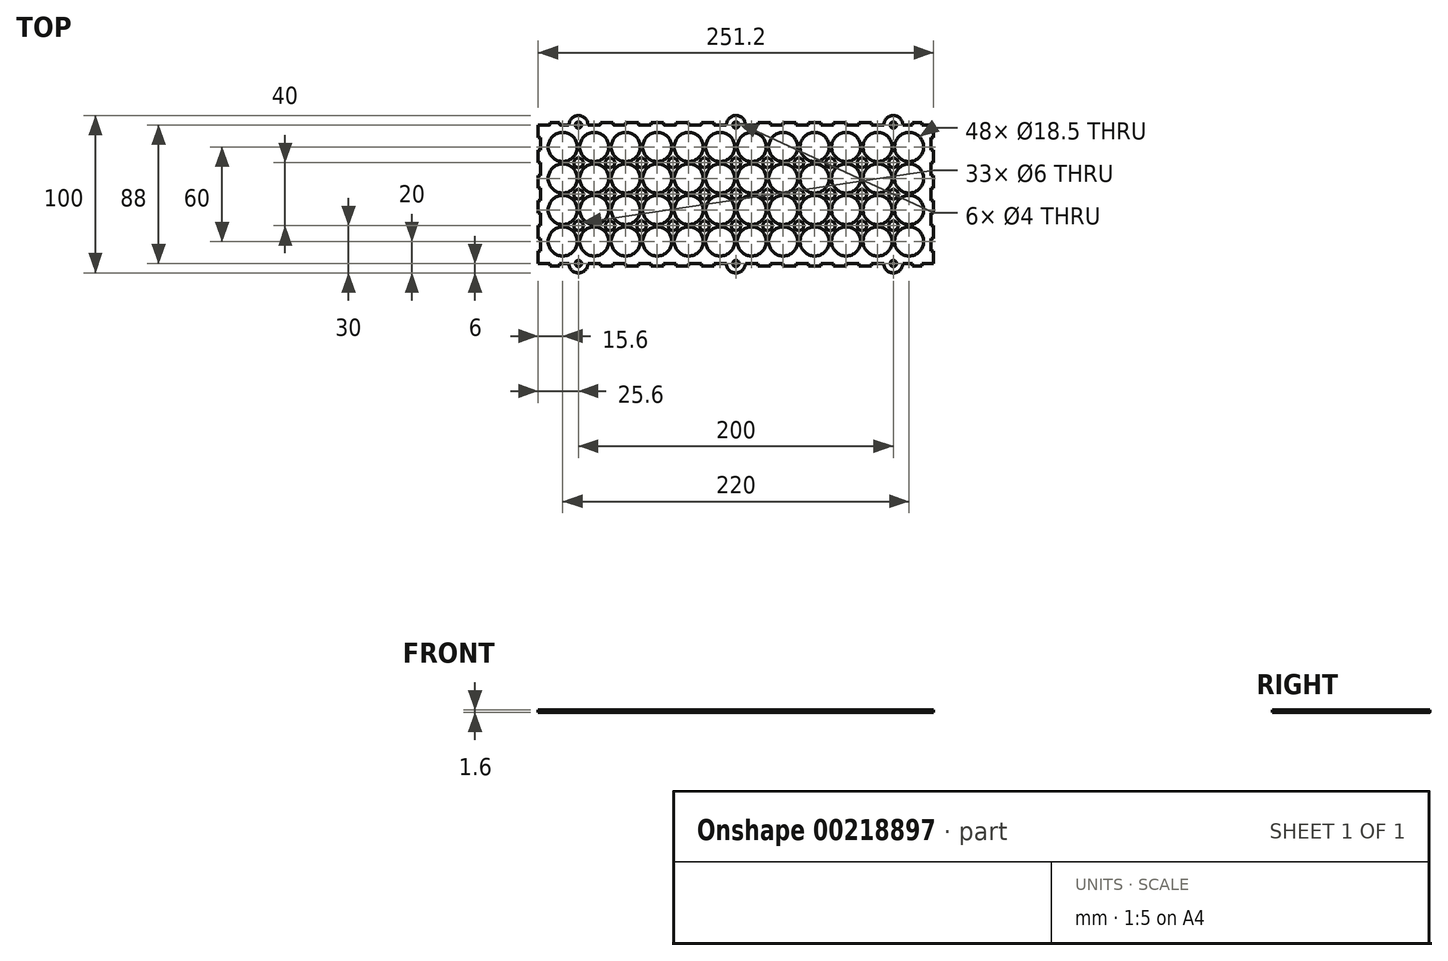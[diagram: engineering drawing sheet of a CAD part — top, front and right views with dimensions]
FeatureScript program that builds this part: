
annotation { "Feature Type Name" : "Feature", "Feature Type Description" : "" }
export const myFeature = defineFeature(function(context is Context, id is Id, definition is map)
    precondition{}
    {
        {
            var Q0;
            Q0=qCreatedBy(makeId("Top.planeOp"),FACE);
            var sketch = newSketch(context, id + "F0", { "sketchPlane" : qUnion([Q0])});
            skCircle(sketch, "E0", {"center": v(-110, -30) * mm, "radius": 9.25 * mm});
            skCircle(sketch, "E1.0.1.0", {"center": v(-110, -10) * mm, "radius": 9.25 * mm});
            skCircle(sketch, "E1.0.2.0", {"center": v(-110, 10) * mm, "radius": 9.25 * mm});
            skCircle(sketch, "E1.0.3.0", {"center": v(-110, 30) * mm, "radius": 9.25 * mm});
            skCircle(sketch, "E1.1.0.0", {"center": v(-90, -30) * mm, "radius": 9.25 * mm});
            skCircle(sketch, "E1.1.1.0", {"center": v(-90, -10) * mm, "radius": 9.25 * mm});
            skCircle(sketch, "E1.1.2.0", {"center": v(-90, 10) * mm, "radius": 9.25 * mm});
            skCircle(sketch, "E1.1.3.0", {"center": v(-90, 30) * mm, "radius": 9.25 * mm});
            skCircle(sketch, "E1.2.0.0", {"center": v(-70, -30) * mm, "radius": 9.25 * mm});
            skCircle(sketch, "E1.2.1.0", {"center": v(-70, -10) * mm, "radius": 9.25 * mm});
            skCircle(sketch, "E1.2.2.0", {"center": v(-70, 10) * mm, "radius": 9.25 * mm});
            skCircle(sketch, "E1.2.3.0", {"center": v(-70, 30) * mm, "radius": 9.25 * mm});
            skCircle(sketch, "E1.3.0.0", {"center": v(-50, -30) * mm, "radius": 9.25 * mm});
            skCircle(sketch, "E1.3.1.0", {"center": v(-50, -10) * mm, "radius": 9.25 * mm});
            skCircle(sketch, "E1.3.2.0", {"center": v(-50, 10) * mm, "radius": 9.25 * mm});
            skCircle(sketch, "E1.3.3.0", {"center": v(-50, 30) * mm, "radius": 9.25 * mm});
            skCircle(sketch, "E1.4.0.0", {"center": v(-30, -30) * mm, "radius": 9.25 * mm});
            skCircle(sketch, "E1.4.1.0", {"center": v(-30, -10) * mm, "radius": 9.25 * mm});
            skCircle(sketch, "E1.4.2.0", {"center": v(-30, 10) * mm, "radius": 9.25 * mm});
            skCircle(sketch, "E1.4.3.0", {"center": v(-30, 30) * mm, "radius": 9.25 * mm});
            skCircle(sketch, "E1.5.0.0", {"center": v(-10, -30) * mm, "radius": 9.25 * mm});
            skCircle(sketch, "E1.5.1.0", {"center": v(-10, -10) * mm, "radius": 9.25 * mm});
            skCircle(sketch, "E1.5.2.0", {"center": v(-10, 10) * mm, "radius": 9.25 * mm});
            skCircle(sketch, "E1.5.3.0", {"center": v(-10, 30) * mm, "radius": 9.25 * mm});
            skCircle(sketch, "E1.6.0.0", {"center": v(10, -30) * mm, "radius": 9.25 * mm});
            skCircle(sketch, "E1.6.1.0", {"center": v(10, -10) * mm, "radius": 9.25 * mm});
            skCircle(sketch, "E1.6.2.0", {"center": v(10, 10) * mm, "radius": 9.25 * mm});
            skCircle(sketch, "E1.6.3.0", {"center": v(10, 30) * mm, "radius": 9.25 * mm});
            skCircle(sketch, "E1.7.0.0", {"center": v(30, -30) * mm, "radius": 9.25 * mm});
            skCircle(sketch, "E1.7.1.0", {"center": v(30, -10) * mm, "radius": 9.25 * mm});
            skCircle(sketch, "E1.7.2.0", {"center": v(30, 10) * mm, "radius": 9.25 * mm});
            skCircle(sketch, "E1.7.3.0", {"center": v(30, 30) * mm, "radius": 9.25 * mm});
            skCircle(sketch, "E1.8.0.0", {"center": v(50, -30) * mm, "radius": 9.25 * mm});
            skCircle(sketch, "E1.8.1.0", {"center": v(50, -10) * mm, "radius": 9.25 * mm});
            skCircle(sketch, "E1.8.2.0", {"center": v(50, 10) * mm, "radius": 9.25 * mm});
            skCircle(sketch, "E1.8.3.0", {"center": v(50, 30) * mm, "radius": 9.25 * mm});
            skCircle(sketch, "E1.9.0.0", {"center": v(70, -30) * mm, "radius": 9.25 * mm});
            skCircle(sketch, "E1.9.1.0", {"center": v(70, -10) * mm, "radius": 9.25 * mm});
            skCircle(sketch, "E1.9.2.0", {"center": v(70, 10) * mm, "radius": 9.25 * mm});
            skCircle(sketch, "E1.9.3.0", {"center": v(70, 30) * mm, "radius": 9.25 * mm});
            skCircle(sketch, "E1.10.0.0", {"center": v(90, -30) * mm, "radius": 9.25 * mm});
            skCircle(sketch, "E1.10.1.0", {"center": v(90, -10) * mm, "radius": 9.25 * mm});
            skCircle(sketch, "E1.10.2.0", {"center": v(90, 10) * mm, "radius": 9.25 * mm});
            skCircle(sketch, "E1.10.3.0", {"center": v(90, 30) * mm, "radius": 9.25 * mm});
            skCircle(sketch, "E1.11.0.0", {"center": v(110, -30) * mm, "radius": 9.25 * mm});
            skCircle(sketch, "E1.11.1.0", {"center": v(110, -10) * mm, "radius": 9.25 * mm});
            skCircle(sketch, "E1.11.2.0", {"center": v(110, 10) * mm, "radius": 9.25 * mm});
            skCircle(sketch, "E1.11.3.0", {"center": v(110, 30) * mm, "radius": 9.25 * mm});
            skLineSegment(sketch, "E1.direction1", {"start": v(-110, -30) * mm, "end": v(-90, -30) * mm, "construction": true});
            skLineSegment(sketch, "E1.direction2", {"start": v(-110, -30) * mm, "end": v(-110, -10) * mm, "construction": true});
            skCircle(sketch, "E2", {"center": v(-100, -20) * mm, "radius": 3 * mm});
            skCircle(sketch, "E3.0.1.0", {"center": v(-100, 0) * mm, "radius": 3 * mm});
            skCircle(sketch, "E3.0.2.0", {"center": v(-100, 20) * mm, "radius": 3 * mm});
            skCircle(sketch, "E3.1.0.0", {"center": v(-80, -20) * mm, "radius": 3 * mm});
            skCircle(sketch, "E3.1.1.0", {"center": v(-80, 0) * mm, "radius": 3 * mm});
            skCircle(sketch, "E3.1.2.0", {"center": v(-80, 20) * mm, "radius": 3 * mm});
            skCircle(sketch, "E3.2.0.0", {"center": v(-60, -20) * mm, "radius": 3 * mm});
            skCircle(sketch, "E3.2.1.0", {"center": v(-60, 0) * mm, "radius": 3 * mm});
            skCircle(sketch, "E3.2.2.0", {"center": v(-60, 20) * mm, "radius": 3 * mm});
            skCircle(sketch, "E3.3.0.0", {"center": v(-40, -20) * mm, "radius": 3 * mm});
            skCircle(sketch, "E3.3.1.0", {"center": v(-40, 0) * mm, "radius": 3 * mm});
            skCircle(sketch, "E3.3.2.0", {"center": v(-40, 20) * mm, "radius": 3 * mm});
            skCircle(sketch, "E3.4.0.0", {"center": v(-20, -20) * mm, "radius": 3 * mm});
            skCircle(sketch, "E3.4.1.0", {"center": v(-20, 0) * mm, "radius": 3 * mm});
            skCircle(sketch, "E3.4.2.0", {"center": v(-20, 20) * mm, "radius": 3 * mm});
            skCircle(sketch, "E3.5.0.0", {"center": v(0, -20) * mm, "radius": 3 * mm});
            skCircle(sketch, "E3.5.1.0", {"center": v(0, 0) * mm, "radius": 3 * mm});
            skCircle(sketch, "E3.5.2.0", {"center": v(0, 20) * mm, "radius": 3 * mm});
            skCircle(sketch, "E3.6.0.0", {"center": v(20, -20) * mm, "radius": 3 * mm});
            skCircle(sketch, "E3.6.1.0", {"center": v(20, 0) * mm, "radius": 3 * mm});
            skCircle(sketch, "E3.6.2.0", {"center": v(20, 20) * mm, "radius": 3 * mm});
            skCircle(sketch, "E3.7.0.0", {"center": v(40, -20) * mm, "radius": 3 * mm});
            skCircle(sketch, "E3.7.1.0", {"center": v(40, 0) * mm, "radius": 3 * mm});
            skCircle(sketch, "E3.7.2.0", {"center": v(40, 20) * mm, "radius": 3 * mm});
            skCircle(sketch, "E3.8.0.0", {"center": v(60, -20) * mm, "radius": 3 * mm});
            skCircle(sketch, "E3.8.1.0", {"center": v(60, 0) * mm, "radius": 3 * mm});
            skCircle(sketch, "E3.8.2.0", {"center": v(60, 20) * mm, "radius": 3 * mm});
            skCircle(sketch, "E3.9.0.0", {"center": v(80, -20) * mm, "radius": 3 * mm});
            skCircle(sketch, "E3.9.1.0", {"center": v(80, 0) * mm, "radius": 3 * mm});
            skCircle(sketch, "E3.9.2.0", {"center": v(80, 20) * mm, "radius": 3 * mm});
            skCircle(sketch, "E3.10.0.0", {"center": v(100, -20) * mm, "radius": 3 * mm});
            skCircle(sketch, "E3.10.1.0", {"center": v(100, 0) * mm, "radius": 3 * mm});
            skCircle(sketch, "E3.10.2.0", {"center": v(100, 20) * mm, "radius": 3 * mm});
            skLineSegment(sketch, "E3.direction1", {"start": v(-100, -20) * mm, "end": v(-80, -20) * mm, "construction": true});
            skLineSegment(sketch, "E3.direction2", {"start": v(-100, -20) * mm, "end": v(-100, 0) * mm, "construction": true});
            skLineSegment(sketch, "E4", {"start": v(-132.11, 0) * mm, "end": v(153.17, 0) * mm, "construction": true});
            skLineSegment(sketch, "E5", {"start": v(0, 71.44) * mm, "end": v(0, -47.17) * mm, "construction": true});
            skCircle(sketch, "E6", {"center": v(0, 44) * mm, "radius": 2 * mm});
            skLineSegment(sketch, "E7", {"start": v(-100, 72.52) * mm, "end": v(-100, -46.79) * mm, "construction": true});
            skLineSegment(sketch, "E8.MirrorCS", {"start": v(100, 72.52) * mm, "end": v(100, -46.79) * mm, "construction": true});
            skCircle(sketch, "E9", {"center": v(-100, 44) * mm, "radius": 2 * mm});
            skCircle(sketch, "E10.MirrorC", {"center": v(100, 44) * mm, "radius": 2 * mm});
            skArc(sketch, "E11", {"start": v(-105.98, 44.46) * mm, "mid": v(-100, 50) * mm, "end": v(-94.02, 44.46) * mm});
            skArc(sketch, "E12.MirrorCS", {"start": v(106, 44) * mm, "mid": v(100, 50) * mm, "end": v(94, 44) * mm});
            skArc(sketch, "E13", {"start": v(-5.98, 44.46) * mm, "mid": v(0.23, 50) * mm, "end": v(6, 44) * mm});
            skLineSegment(sketch, "E14", {"start": v(-106.48, 44) * mm, "end": v(-111.5, 44) * mm});
            skLineSegment(sketch, "E15", {"start": v(-93.52, 44) * mm, "end": v(-86.5, 44) * mm});
            skLineSegment(sketch, "E16", {"start": v(-118, 44.5) * mm, "end": v(-118, 45.6) * mm});
            skLineSegment(sketch, "E17", {"start": v(-118, 45.6) * mm, "end": v(-112, 45.6) * mm});
            skLineSegment(sketch, "E18", {"start": v(-112, 45.6) * mm, "end": v(-112, 44.5) * mm});
            skLineSegment(sketch, "E19", {"start": v(-86, 44.5) * mm, "end": v(-86, 45.6) * mm});
            skLineSegment(sketch, "E20", {"start": v(-86, 45.6) * mm, "end": v(-78, 45.6) * mm});
            skLineSegment(sketch, "E21", {"start": v(-78, 45.6) * mm, "end": v(-78, 44.5) * mm});
            skLineSegment(sketch, "E22.1.0.0", {"start": v(-77.5, 44) * mm, "end": v(-70.5, 44) * mm});
            skLineSegment(sketch, "E22.1.0.1", {"start": v(-70, 44.5) * mm, "end": v(-70, 45.6) * mm});
            skLineSegment(sketch, "E22.1.0.2", {"start": v(-70, 45.6) * mm, "end": v(-62, 45.6) * mm});
            skLineSegment(sketch, "E22.1.0.3", {"start": v(-62, 45.6) * mm, "end": v(-62, 44.5) * mm});
            skLineSegment(sketch, "E22.2.0.0", {"start": v(-61.5, 44) * mm, "end": v(-54, 44) * mm});
            skLineSegment(sketch, "E22.2.0.1", {"start": v(-54, 44) * mm, "end": v(-54, 45.6) * mm});
            skLineSegment(sketch, "E22.2.0.2", {"start": v(-54, 45.6) * mm, "end": v(-46, 45.6) * mm});
            skLineSegment(sketch, "E22.2.0.3", {"start": v(-46, 45.6) * mm, "end": v(-46, 44.5) * mm});
            skLineSegment(sketch, "E22.3.0.0", {"start": v(-45.5, 44) * mm, "end": v(-38.5, 44) * mm});
            skLineSegment(sketch, "E22.3.0.1", {"start": v(-38, 44.5) * mm, "end": v(-38, 45.6) * mm});
            skLineSegment(sketch, "E22.3.0.2", {"start": v(-38, 45.6) * mm, "end": v(-30, 45.6) * mm});
            skLineSegment(sketch, "E22.3.0.3", {"start": v(-30, 45.6) * mm, "end": v(-30, 44.5) * mm});
            skLineSegment(sketch, "E22.4.0.0", {"start": v(-29.5, 44) * mm, "end": v(-22.5, 44) * mm});
            skLineSegment(sketch, "E22.4.0.1", {"start": v(-22, 44.5) * mm, "end": v(-22, 45.6) * mm});
            skLineSegment(sketch, "E22.4.0.2", {"start": v(-22, 45.6) * mm, "end": v(-14, 45.6) * mm});
            skLineSegment(sketch, "E22.4.0.3", {"start": v(-14, 45.6) * mm, "end": v(-14, 44.5) * mm});
            skLineSegment(sketch, "E22.direction1", {"start": v(-94, 44) * mm, "end": v(-78, 44) * mm, "construction": true});
            skLineSegment(sketch, "E23", {"start": v(-13.5, 44) * mm, "end": v(-6.48, 44) * mm});
            skLineSegment(sketch, "E24.MirrorCS", {"start": v(30, 45.6) * mm, "end": v(30, 44) * mm});
            skLineSegment(sketch, "E25.MirrorCS", {"start": v(38, 44) * mm, "end": v(38, 45.6) * mm});
            skLineSegment(sketch, "E26.MirrorCS", {"start": v(54, 44) * mm, "end": v(54, 45.6) * mm});
            skLineSegment(sketch, "E27.MirrorCS", {"start": v(14, 45.6) * mm, "end": v(14, 44.5) * mm});
            skLineSegment(sketch, "E28.MirrorCS", {"start": v(78, 45.6) * mm, "end": v(78, 44) * mm});
            skLineSegment(sketch, "E29.MirrorCS", {"start": v(46, 45.6) * mm, "end": v(46, 44) * mm});
            skLineSegment(sketch, "E30.MirrorCS", {"start": v(62, 45.6) * mm, "end": v(62, 44) * mm});
            skLineSegment(sketch, "E31.MirrorCS", {"start": v(86, 44) * mm, "end": v(86, 45.6) * mm});
            skLineSegment(sketch, "E32.MirrorCS", {"start": v(22, 44) * mm, "end": v(22, 45.6) * mm});
            skLineSegment(sketch, "E33.MirrorCS", {"start": v(70, 44) * mm, "end": v(70, 45.6) * mm});
            skLineSegment(sketch, "E34.MirrorCS", {"start": v(94, 44) * mm, "end": v(86, 44) * mm});
            skLineSegment(sketch, "E35.MirrorCS", {"start": v(38, 45.6) * mm, "end": v(30, 45.6) * mm});
            skLineSegment(sketch, "E36.MirrorCS", {"start": v(30, 44) * mm, "end": v(22, 44) * mm});
            skLineSegment(sketch, "E37.MirrorCS", {"start": v(22, 45.6) * mm, "end": v(14, 45.6) * mm});
            skLineSegment(sketch, "E38.MirrorCS", {"start": v(62, 44) * mm, "end": v(54, 44) * mm});
            skLineSegment(sketch, "E39.MirrorCS", {"start": v(70, 45.6) * mm, "end": v(62, 45.6) * mm});
            skLineSegment(sketch, "E40.MirrorCS", {"start": v(46, 44) * mm, "end": v(38, 44) * mm});
            skLineSegment(sketch, "E41.MirrorCS", {"start": v(78, 44) * mm, "end": v(70, 44) * mm});
            skLineSegment(sketch, "E42.MirrorCS", {"start": v(86, 45.6) * mm, "end": v(78, 45.6) * mm});
            skLineSegment(sketch, "E43.MirrorCS", {"start": v(13.5, 44) * mm, "end": v(6, 44) * mm});
            skLineSegment(sketch, "E44.MirrorCS", {"start": v(54, 45.6) * mm, "end": v(46, 45.6) * mm});
            skLineSegment(sketch, "E45.MirrorCS", {"start": v(14, 45.6) * mm, "end": v(14, 44) * mm});
            skLineSegment(sketch, "E46.MirrorCS", {"start": v(14, 44) * mm, "end": v(6, 44) * mm});
            skLineSegment(sketch, "E47.MirrorCS", {"start": v(94, 44) * mm, "end": v(78, 44) * mm, "construction": true});
            skLineSegment(sketch, "E48", {"start": v(-118.5, 44) * mm, "end": v(-124, 44) * mm});
            skLineSegment(sketch, "E49.MirrorCS", {"start": v(118, 45.6) * mm, "end": v(112, 45.6) * mm});
            skLineSegment(sketch, "E50.MirrorCS", {"start": v(118, 44) * mm, "end": v(118, 45.6) * mm});
            skLineSegment(sketch, "E51.MirrorCS", {"start": v(112, 45.6) * mm, "end": v(112, 44) * mm});
            skLineSegment(sketch, "E52.MirrorCS", {"start": v(106, 44) * mm, "end": v(112, 44) * mm});
            skLineSegment(sketch, "E53.MirrorCS", {"start": v(118, 44) * mm, "end": v(124, 44) * mm});
            skLineSegment(sketch, "E54.MirrorCS", {"start": v(78, -45.6) * mm, "end": v(78, -44) * mm});
            skLineSegment(sketch, "E55.MirrorCS", {"start": v(86, -44) * mm, "end": v(86, -45.6) * mm});
            skLineSegment(sketch, "E56.MirrorCS", {"start": v(22, -44) * mm, "end": v(22, -45.6) * mm});
            skLineSegment(sketch, "E57.MirrorCS", {"start": v(70, -44) * mm, "end": v(70, -45.6) * mm});
            skLineSegment(sketch, "E58.MirrorCS", {"start": v(46, -45.6) * mm, "end": v(46, -44) * mm});
            skLineSegment(sketch, "E59.MirrorCS", {"start": v(62, -45.6) * mm, "end": v(62, -44) * mm});
            skLineSegment(sketch, "E60.MirrorCS", {"start": v(14, -45.6) * mm, "end": v(14, -44) * mm});
            skLineSegment(sketch, "E61.MirrorCS", {"start": v(54, -44) * mm, "end": v(54, -45.6) * mm});
            skLineSegment(sketch, "E62.MirrorCS", {"start": v(30, -45.6) * mm, "end": v(30, -44) * mm});
            skLineSegment(sketch, "E63.MirrorCS", {"start": v(38, -44) * mm, "end": v(38, -45.6) * mm});
            skLineSegment(sketch, "E64.MirrorCS", {"start": v(-78, -45.6) * mm, "end": v(-78, -44) * mm});
            skLineSegment(sketch, "E65.MirrorCS", {"start": v(-30, -45.6) * mm, "end": v(-30, -44) * mm});
            skLineSegment(sketch, "E66.MirrorCS", {"start": v(94, -44) * mm, "end": v(86, -44) * mm});
            skLineSegment(sketch, "E67.MirrorCS", {"start": v(-112, -45.6) * mm, "end": v(-112, -44) * mm});
            skLineSegment(sketch, "E68.MirrorCS", {"start": v(-22, -44) * mm, "end": v(-22, -45.6) * mm});
            skLineSegment(sketch, "E69.MirrorCS", {"start": v(-86, -44) * mm, "end": v(-86, -45.6) * mm});
            skLineSegment(sketch, "E70.MirrorCS", {"start": v(-46, -45.6) * mm, "end": v(-46, -44) * mm});
            skLineSegment(sketch, "E71.MirrorCS", {"start": v(-70, -44) * mm, "end": v(-70, -45.6) * mm});
            skLineSegment(sketch, "E72.MirrorCS", {"start": v(118, -44) * mm, "end": v(118, -45.6) * mm});
            skLineSegment(sketch, "E73.MirrorCS", {"start": v(112, -45.6) * mm, "end": v(112, -44) * mm});
            skLineSegment(sketch, "E74.MirrorCS", {"start": v(-38, -44) * mm, "end": v(-38, -45.6) * mm});
            skLineSegment(sketch, "E75.MirrorCS", {"start": v(-14, -45.6) * mm, "end": v(-14, -44) * mm});
            skLineSegment(sketch, "E76.MirrorCS", {"start": v(-62, -45.6) * mm, "end": v(-62, -44) * mm});
            skLineSegment(sketch, "E77.MirrorCS", {"start": v(-118, -44) * mm, "end": v(-118, -45.6) * mm});
            skLineSegment(sketch, "E78.MirrorCS", {"start": v(-54, -44) * mm, "end": v(-54, -45.6) * mm});
            skLineSegment(sketch, "E79.MirrorCS", {"start": v(54, -45.6) * mm, "end": v(46, -45.6) * mm});
            skLineSegment(sketch, "E80.MirrorCS", {"start": v(38, -45.6) * mm, "end": v(30, -45.6) * mm});
            skLineSegment(sketch, "E81.MirrorCS", {"start": v(62, -44) * mm, "end": v(54, -44) * mm});
            skLineSegment(sketch, "E82.MirrorCS", {"start": v(-94, -44) * mm, "end": v(-86, -44) * mm});
            skLineSegment(sketch, "E83.MirrorCS", {"start": v(30, -44) * mm, "end": v(22, -44) * mm});
            skLineSegment(sketch, "E84.MirrorCS", {"start": v(86, -45.6) * mm, "end": v(78, -45.6) * mm});
            skLineSegment(sketch, "E85.MirrorCS", {"start": v(70, -45.6) * mm, "end": v(62, -45.6) * mm});
            skLineSegment(sketch, "E86.MirrorCS", {"start": v(22, -45.6) * mm, "end": v(14, -45.6) * mm});
            skLineSegment(sketch, "E87.MirrorCS", {"start": v(46, -44) * mm, "end": v(38, -44) * mm});
            skLineSegment(sketch, "E88.MirrorCS", {"start": v(78, -44) * mm, "end": v(70, -44) * mm});
            skLineSegment(sketch, "E89.MirrorCS", {"start": v(14, -44) * mm, "end": v(6, -44) * mm});
            skLineSegment(sketch, "E90.MirrorCS", {"start": v(-118, -45.6) * mm, "end": v(-112, -45.6) * mm});
            skLineSegment(sketch, "E91.MirrorCS", {"start": v(-30, -44) * mm, "end": v(-22, -44) * mm});
            skLineSegment(sketch, "E92.MirrorCS", {"start": v(-118, -44) * mm, "end": v(-124, -44) * mm});
            skLineSegment(sketch, "E93.MirrorCS", {"start": v(-106, -44) * mm, "end": v(-112, -44) * mm});
            skLineSegment(sketch, "E94.MirrorCS", {"start": v(-46, -44) * mm, "end": v(-38, -44) * mm});
            skArc(sketch, "E95.MirrorCS", {"start": v(-6, -44) * mm, "mid": v(0, -50) * mm, "end": v(6, -44) * mm});
            skLineSegment(sketch, "E96.MirrorCS", {"start": v(100, -72.52) * mm, "end": v(100, 46.79) * mm, "construction": true});
            skLineSegment(sketch, "E97.MirrorCS", {"start": v(-70, -45.6) * mm, "end": v(-62, -45.6) * mm});
            skLineSegment(sketch, "E98.MirrorCS", {"start": v(-100, -72.52) * mm, "end": v(-100, 46.79) * mm, "construction": true});
            skArc(sketch, "E99.MirrorCS", {"start": v(106, -44) * mm, "mid": v(100, -50) * mm, "end": v(94, -44) * mm});
            skCircle(sketch, "E100.MirrorC", {"center": v(0, -44) * mm, "radius": 2 * mm});
            skLineSegment(sketch, "E101.MirrorCS", {"start": v(106, -44) * mm, "end": v(112, -44) * mm});
            skCircle(sketch, "E102.MirrorC", {"center": v(100, -44) * mm, "radius": 2 * mm});
            skLineSegment(sketch, "E103.MirrorCS", {"start": v(-62, -44) * mm, "end": v(-54, -44) * mm});
            skLineSegment(sketch, "E104.MirrorCS", {"start": v(-14, -44) * mm, "end": v(-6, -44) * mm});
            skLineSegment(sketch, "E105.MirrorCS", {"start": v(-54, -45.6) * mm, "end": v(-46, -45.6) * mm});
            skLineSegment(sketch, "E106.MirrorCS", {"start": v(0, -71.44) * mm, "end": v(0, 47.17) * mm, "construction": true});
            skLineSegment(sketch, "E107.MirrorCS", {"start": v(118, -45.6) * mm, "end": v(112, -45.6) * mm});
            skLineSegment(sketch, "E108.MirrorCS", {"start": v(-22, -45.6) * mm, "end": v(-14, -45.6) * mm});
            skLineSegment(sketch, "E109.MirrorCS", {"start": v(-86, -45.6) * mm, "end": v(-78, -45.6) * mm});
            skLineSegment(sketch, "E110.MirrorCS", {"start": v(-94, -44) * mm, "end": v(-78, -44) * mm, "construction": true});
            skLineSegment(sketch, "E111.MirrorCS", {"start": v(-78, -44) * mm, "end": v(-70, -44) * mm});
            skLineSegment(sketch, "E112.MirrorCS", {"start": v(118, -44) * mm, "end": v(124, -44) * mm});
            skCircle(sketch, "E113.MirrorC", {"center": v(-100, -44) * mm, "radius": 2 * mm});
            skLineSegment(sketch, "E114.MirrorCS", {"start": v(-38, -45.6) * mm, "end": v(-30, -45.6) * mm});
            skArc(sketch, "E115.MirrorCS", {"start": v(-106, -44) * mm, "mid": v(-100, -50) * mm, "end": v(-94, -44) * mm});
            skLineSegment(sketch, "E116.MirrorCS", {"start": v(94, -44) * mm, "end": v(78, -44) * mm, "construction": true});
            skLineSegment(sketch, "E117", {"start": v(-124, 44) * mm, "end": v(-125.6, 44) * mm});
            skLineSegment(sketch, "E118", {"start": v(-125.6, 44) * mm, "end": v(-125.6, 36) * mm});
            skLineSegment(sketch, "E119", {"start": v(-125.6, 36) * mm, "end": v(-124, 36) * mm});
            skLineSegment(sketch, "E120", {"start": v(-124, 36) * mm, "end": v(-124, 28) * mm});
            skLineSegment(sketch, "E121.0.1.0", {"start": v(-124, 20) * mm, "end": v(-124, 12) * mm});
            skLineSegment(sketch, "E121.0.1.1", {"start": v(-125.6, 20) * mm, "end": v(-124, 20) * mm});
            skLineSegment(sketch, "E121.0.1.2", {"start": v(-125.6, 28) * mm, "end": v(-125.6, 20) * mm});
            skLineSegment(sketch, "E121.0.1.3", {"start": v(-124, 28) * mm, "end": v(-125.6, 28) * mm});
            skLineSegment(sketch, "E121.0.2.0", {"start": v(-124, 4) * mm, "end": v(-124, -4) * mm});
            skLineSegment(sketch, "E121.0.2.1", {"start": v(-125.6, 4) * mm, "end": v(-124, 4) * mm});
            skLineSegment(sketch, "E121.0.2.2", {"start": v(-125.6, 12) * mm, "end": v(-125.6, 4) * mm});
            skLineSegment(sketch, "E121.0.2.3", {"start": v(-124, 12) * mm, "end": v(-125.6, 12) * mm});
            skLineSegment(sketch, "E121.0.3.0", {"start": v(-124, -12) * mm, "end": v(-124, -20) * mm});
            skLineSegment(sketch, "E121.0.3.1", {"start": v(-125.6, -12) * mm, "end": v(-124, -12) * mm});
            skLineSegment(sketch, "E121.0.3.2", {"start": v(-125.6, -4) * mm, "end": v(-125.6, -12) * mm});
            skLineSegment(sketch, "E121.0.3.3", {"start": v(-124, -4) * mm, "end": v(-125.6, -4) * mm});
            skLineSegment(sketch, "E121.0.4.0", {"start": v(-124, -28) * mm, "end": v(-124, -36) * mm});
            skLineSegment(sketch, "E121.0.4.1", {"start": v(-125.6, -28) * mm, "end": v(-124, -28) * mm});
            skLineSegment(sketch, "E121.0.4.2", {"start": v(-125.6, -20) * mm, "end": v(-125.6, -28) * mm});
            skLineSegment(sketch, "E121.0.4.3", {"start": v(-124, -20) * mm, "end": v(-125.6, -20) * mm});
            skLineSegment(sketch, "E121.direction1", {"start": v(-124, 28) * mm, "end": v(-99, 28) * mm, "construction": true});
            skLineSegment(sketch, "E121.direction2", {"start": v(-124, 28) * mm, "end": v(-124, 12) * mm, "construction": true});
            skLineSegment(sketch, "E122", {"start": v(-124, -36) * mm, "end": v(-125.6, -36) * mm});
            skLineSegment(sketch, "E123", {"start": v(-125.6, -36) * mm, "end": v(-125.6, -44) * mm});
            skLineSegment(sketch, "E124", {"start": v(-125.6, -44) * mm, "end": v(-124, -44) * mm});
            skLineSegment(sketch, "E125.MirrorCS", {"start": v(125.6, -44) * mm, "end": v(124, -44) * mm});
            skLineSegment(sketch, "E126.MirrorCS", {"start": v(124, 28) * mm, "end": v(125.6, 28) * mm});
            skLineSegment(sketch, "E127.MirrorCS", {"start": v(125.6, 20) * mm, "end": v(124, 20) * mm});
            skLineSegment(sketch, "E128.MirrorCS", {"start": v(124, -20) * mm, "end": v(125.6, -20) * mm});
            skLineSegment(sketch, "E129.MirrorCS", {"start": v(125.6, -12) * mm, "end": v(124, -12) * mm});
            skLineSegment(sketch, "E130.MirrorCS", {"start": v(124, -4) * mm, "end": v(125.6, -4) * mm});
            skLineSegment(sketch, "E131.MirrorCS", {"start": v(124, 44) * mm, "end": v(125.6, 44) * mm});
            skLineSegment(sketch, "E132.MirrorCS", {"start": v(125.6, -28) * mm, "end": v(124, -28) * mm});
            skLineSegment(sketch, "E133.MirrorCS", {"start": v(124, -36) * mm, "end": v(125.6, -36) * mm});
            skLineSegment(sketch, "E134.MirrorCS", {"start": v(124, 12) * mm, "end": v(125.6, 12) * mm});
            skLineSegment(sketch, "E135.MirrorCS", {"start": v(125.6, 4) * mm, "end": v(124, 4) * mm});
            skLineSegment(sketch, "E136.MirrorCS", {"start": v(125.6, 36) * mm, "end": v(124, 36) * mm});
            skLineSegment(sketch, "E137.MirrorCS", {"start": v(124, 20) * mm, "end": v(124, 12) * mm});
            skLineSegment(sketch, "E138.MirrorCS", {"start": v(124, 4) * mm, "end": v(124, -4) * mm});
            skLineSegment(sketch, "E139.MirrorCS", {"start": v(125.6, -36) * mm, "end": v(125.6, -44) * mm});
            skLineSegment(sketch, "E140.MirrorCS", {"start": v(124, 28) * mm, "end": v(124, 12) * mm, "construction": true});
            skLineSegment(sketch, "E141.MirrorCS", {"start": v(124, 36) * mm, "end": v(124, 28) * mm});
            skLineSegment(sketch, "E142.MirrorCS", {"start": v(125.6, 12) * mm, "end": v(125.6, 4) * mm});
            skLineSegment(sketch, "E143.MirrorCS", {"start": v(125.6, -20) * mm, "end": v(125.6, -28) * mm});
            skLineSegment(sketch, "E144.MirrorCS", {"start": v(124, -28) * mm, "end": v(124, -36) * mm});
            skLineSegment(sketch, "E145.MirrorCS", {"start": v(125.6, 44) * mm, "end": v(125.6, 36) * mm});
            skLineSegment(sketch, "E146.MirrorCS", {"start": v(125.6, 28) * mm, "end": v(125.6, 20) * mm});
            skLineSegment(sketch, "E147.MirrorCS", {"start": v(125.6, -4) * mm, "end": v(125.6, -12) * mm});
            skLineSegment(sketch, "E148.MirrorCS", {"start": v(124, -12) * mm, "end": v(124, -20) * mm});
            skCircle(sketch, "E149", {"center": v(0, 44) * mm, "radius": 7.95 * mm, "construction": true});
            skPoint(sketch, "E150.visualSharp", {"position": v(-118, 44) * mm});
            skArc(sketch, "E150.filletArc", {"start": v(-118.5, 44) * mm, "mid": v(-118.15, 44.15) * mm, "end": v(-118, 44.5) * mm});
            skPoint(sketch, "E151.visualSharp", {"position": v(-112, 44) * mm});
            skArc(sketch, "E151.filletArc", {"start": v(-112, 44.5) * mm, "mid": v(-111.85, 44.15) * mm, "end": v(-111.5, 44) * mm});
            skPoint(sketch, "E152.visualSharp", {"position": v(-106, 44) * mm});
            skArc(sketch, "E152.filletArc", {"start": v(-106.48, 44) * mm, "mid": v(-106.14, 44.13) * mm, "end": v(-105.98, 44.46) * mm});
            skPoint(sketch, "E153.visualSharp", {"position": v(-94, 44) * mm});
            skArc(sketch, "E153.filletArc", {"start": v(-94.02, 44.46) * mm, "mid": v(-93.86, 44.13) * mm, "end": v(-93.52, 44) * mm});
            skPoint(sketch, "E154.visualSharp", {"position": v(-86, 44) * mm});
            skArc(sketch, "E154.filletArc", {"start": v(-86.5, 44) * mm, "mid": v(-86.15, 44.15) * mm, "end": v(-86, 44.5) * mm});
            skPoint(sketch, "E155.visualSharp", {"position": v(-78, 44) * mm});
            skArc(sketch, "E155.filletArc", {"start": v(-78, 44.5) * mm, "mid": v(-77.85, 44.15) * mm, "end": v(-77.5, 44) * mm});
            skPoint(sketch, "E156.visualSharp", {"position": v(-70, 44) * mm});
            skArc(sketch, "E156.filletArc", {"start": v(-70.5, 44) * mm, "mid": v(-70.15, 44.15) * mm, "end": v(-70, 44.5) * mm});
            skPoint(sketch, "E157.visualSharp", {"position": v(-62, 44) * mm});
            skArc(sketch, "E157.filletArc", {"start": v(-62, 44.5) * mm, "mid": v(-61.85, 44.15) * mm, "end": v(-61.5, 44) * mm});
            skPoint(sketch, "E158.visualSharp", {"position": v(-46, 44) * mm});
            skArc(sketch, "E158.filletArc", {"start": v(-46, 44.5) * mm, "mid": v(-45.85, 44.15) * mm, "end": v(-45.5, 44) * mm});
            skPoint(sketch, "E159.visualSharp", {"position": v(-38, 44) * mm});
            skArc(sketch, "E159.filletArc", {"start": v(-38.5, 44) * mm, "mid": v(-38.15, 44.15) * mm, "end": v(-38, 44.5) * mm});
            skPoint(sketch, "E160.visualSharp", {"position": v(-30, 44) * mm});
            skArc(sketch, "E160.filletArc", {"start": v(-30, 44.5) * mm, "mid": v(-29.85, 44.15) * mm, "end": v(-29.5, 44) * mm});
            skPoint(sketch, "E161.visualSharp", {"position": v(-22, 44) * mm});
            skArc(sketch, "E161.filletArc", {"start": v(-22.5, 44) * mm, "mid": v(-22.15, 44.15) * mm, "end": v(-22, 44.5) * mm});
            skPoint(sketch, "E162.visualSharp", {"position": v(-14, 44) * mm});
            skArc(sketch, "E162.filletArc", {"start": v(-14, 44.5) * mm, "mid": v(-13.85, 44.15) * mm, "end": v(-13.5, 44) * mm});
            skPoint(sketch, "E163.visualSharp", {"position": v(-6, 44) * mm});
            skArc(sketch, "E163.filletArc", {"start": v(-6.48, 44) * mm, "mid": v(-6.14, 44.13) * mm, "end": v(-5.98, 44.46) * mm});
            skPoint(sketch, "E164.visualSharp", {"position": v(14, 44) * mm});
            skArc(sketch, "E164.filletArc", {"start": v(13.5, 44) * mm, "mid": v(13.85, 44.15) * mm, "end": v(14, 44.5) * mm});
            skSolve(sketch);
        }
        {
            var Q0;
            Q0=makeQuery(id+"F0.imprint","IMPRINT",FACE,{"disambiguationData":[TD([[makeQuery(id+"F0.imprint","IMPRINT",EDGE,{"derivedFrom":sQuery(id+"F0.wireOp",EDGE,"E0")}),-1.0]])]});
            extrude(context, id + "F1", {"entities" : qUnion([Q0]), "depth" : 1.6 * mm});
        }
    });
